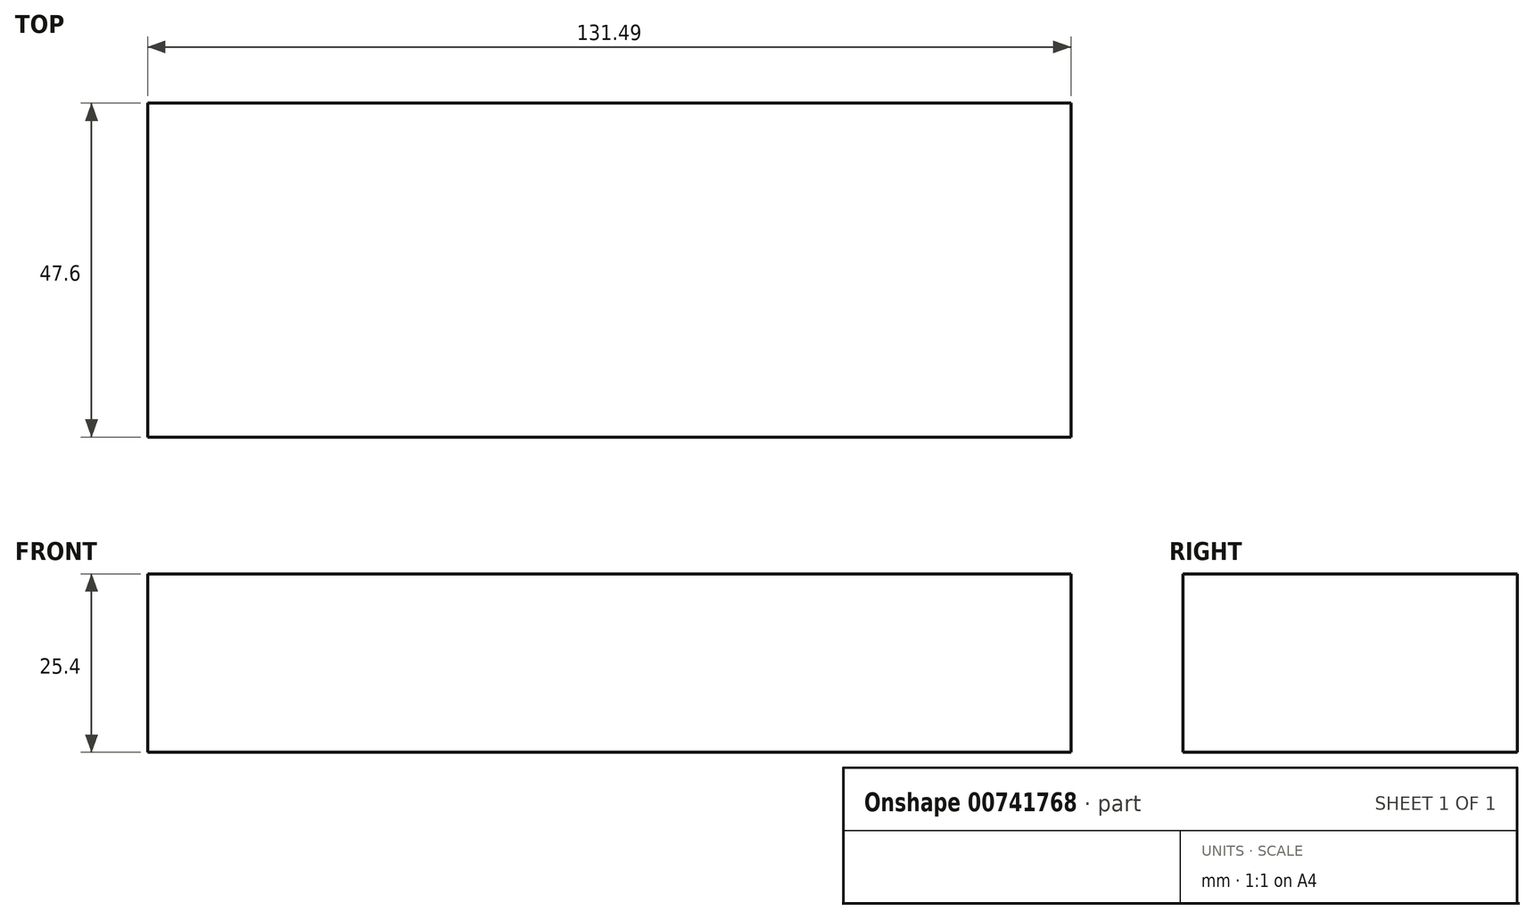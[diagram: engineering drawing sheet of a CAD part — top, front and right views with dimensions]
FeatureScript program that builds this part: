
annotation { "Feature Type Name" : "Feature", "Feature Type Description" : "" }
export const myFeature = defineFeature(function(context is Context, id is Id, definition is map)
    precondition{}
    {
        {
            var Q0;
            Q0=qCreatedBy(makeId("Top.planeOp"),FACE);
            var sketch = newSketch(context, id + "F0", { "sketchPlane" : qUnion([Q0])});
            skLineSegment(sketch, "E0.bottom", {"start": v(-61.02, -47.6) * mm, "end": v(70.47, -47.6) * mm});
            skLineSegment(sketch, "E0.top", {"start": v(-61.02, 0) * mm, "end": v(70.47, 0) * mm});
            skLineSegment(sketch, "E0.left", {"start": v(-61.02, -47.6) * mm, "end": v(-61.02, 0) * mm});
            skLineSegment(sketch, "E0.right", {"start": v(70.47, -47.6) * mm, "end": v(70.47, 0) * mm});
            skSolve(sketch);
        }
        {
            var Q0;
            Q0=makeQuery(id+"F0.imprint","IMPRINT",FACE,{"disambiguationData":[TD([[makeQuery(id+"F0.imprint","IMPRINT",EDGE,{"derivedFrom":sQuery(id+"F0.wireOp",EDGE,"E0.bottom")}),1.0]])]});
            extrude(context, id + "F1", {"entities" : qUnion([Q0]), "depth" : 25.4 * mm, "offsetDistance" : 25.4 * mm});
        }
    });
